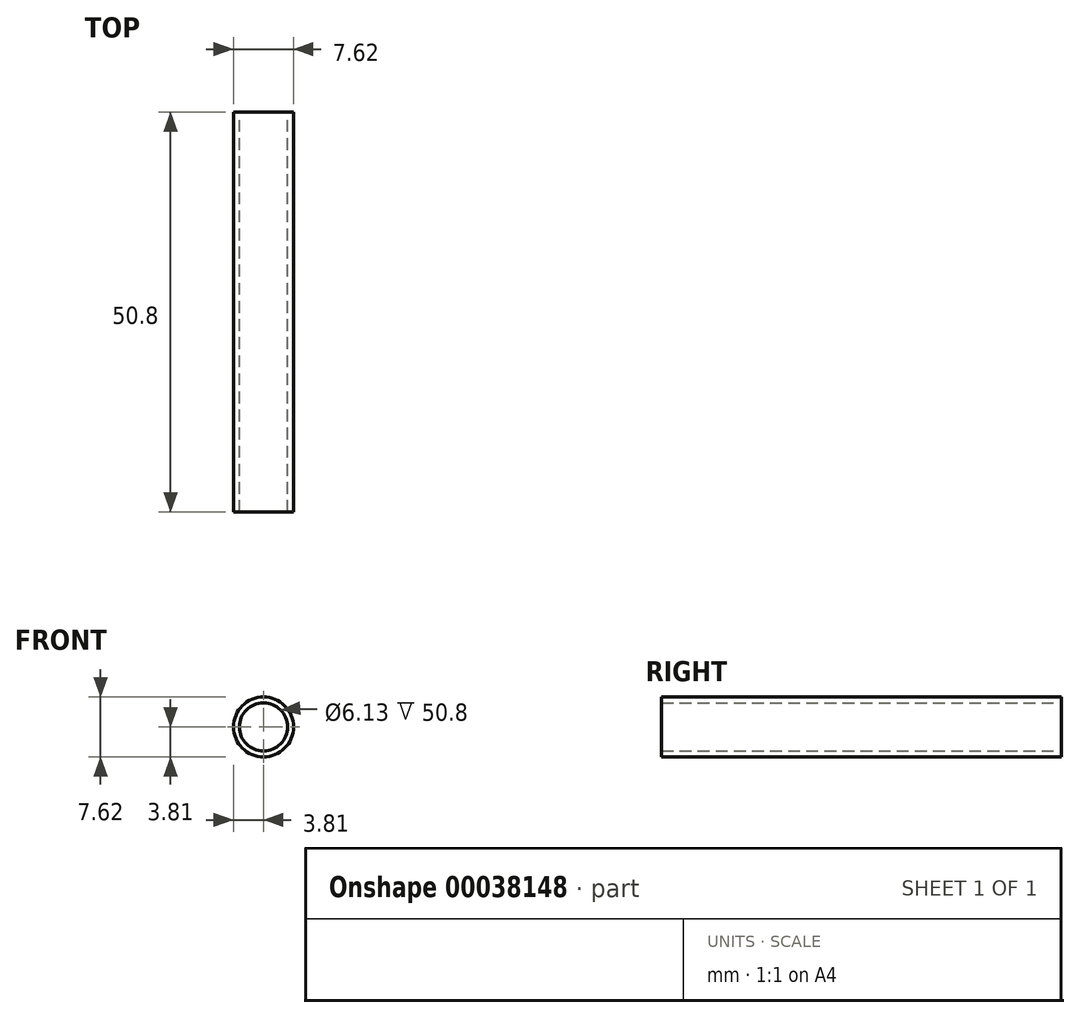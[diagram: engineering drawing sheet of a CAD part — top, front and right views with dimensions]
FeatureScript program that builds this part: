
annotation { "Feature Type Name" : "Feature", "Feature Type Description" : "" }
export const myFeature = defineFeature(function(context is Context, id is Id, definition is map)
    precondition{}
    {
        {
            var Q0;
            Q0=qCreatedBy(makeId("Front.planeOp"),FACE);
            var sketch = newSketch(context, id + "F0", { "sketchPlane" : qUnion([Q0])});
            skCircle(sketch, "E0", {"center": v(0, 0) * mm, "radius": 3.81 * mm});
            skSolve(sketch);
        }
        {
            var Q0;
            Q0=makeQuery(id+"F0.imprint","IMPRINT",FACE,{"disambiguationData":[TD([[makeQuery(id+"F0.imprint","IMPRINT",EDGE,{"derivedFrom":sQuery(id+"F0.wireOp",EDGE,"E0")}),1.0]])]});
            extrude(context, id + "F1", {"entities" : qUnion([Q0]), "depth" : 25.4 * mm});
        }
        {
            var Q0;
            Q0=sQuery(id+"F0.wireOp",EDGE,"E0");
            extrude(context, id + "F2", {"bodyType" : ToolBodyType.SURFACE, "surfaceEntities" : qUnion([Q0]), "depth" : 25.4 * mm});
        }
        {
            var Q0;
            Q0=makeQuery(id+"F1.opExtrude","CAP_FACE",FACE,{"disambiguationData":[OSD([sQuery(id+"F0.wireOp",EDGE,"E0")])],"isStart":true});
            extrude(context, id + "F3", {"entities" : qUnion([Q0]), "operationType" : NewBodyOperationType.ADD, "depth" : 25.4 * mm});
        }
        {
            var Q0;
            Q0=makeQuery(id+"F3.opExtrude","CAP_FACE",FACE,{"disambiguationData":[OSD([sQuery(id+"F0.wireOp",EDGE,"E0")])],"isStart":false});
            var sketch = newSketch(context, id + "F4", { "sketchPlane" : qUnion([Q0])});
            skCircle(sketch, "E1", {"center": v(0, 0) * mm, "radius": 3.06 * mm});
            skSolve(sketch);
        }
        {
            var Q0;
            Q0=makeQuery(id+"F4.imprint","IMPRINT",FACE,{"disambiguationData":[TD([[makeQuery(id+"F4.imprint","IMPRINT",EDGE,{"derivedFrom":sQuery(id+"F4.wireOp",EDGE,"E1")}),1.0]])]});
            extrude(context, id + "F5", {"entities" : qUnion([Q0]), "operationType" : NewBodyOperationType.REMOVE, "endBound" : BoundingType.THROUGH_ALL, "oppositeDirection" : true, "depth" : 25.4 * mm});
        }
    });
